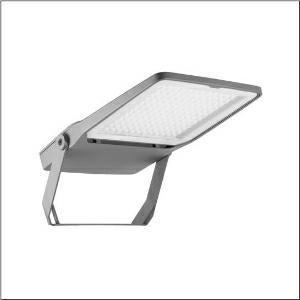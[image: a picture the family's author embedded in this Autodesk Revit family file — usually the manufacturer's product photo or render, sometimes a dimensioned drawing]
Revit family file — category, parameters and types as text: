
# Revit family: floodlight_fl_20_midi___pl61_5xa7681e2c1ac_9e02
name_source: partatom
category: Lighting Fixtures
units: mm (PartAtom-declared; Revit-internal decimal feet)

## family parameters
Cut with Voids When Loaded = No
Host = Face
Light Source = No
Part Type = Normal
Room Calculation Point = No
Round Connector Dimension = Use Diameter
Shared = No

## types (1)
- Floodlight FL 20 midi  PL61 (1 x LED 4000K / CRI = 70 (unbekannt), 27150 lm, 4000K)
    Apparent Load = 208 VA
    CIE Flux Codes = 33 65 98 100 100
    Color Rendering = 70
    Color Temperature = 4000K
    Default Elevation = 1800 mm
    Description = Floodlight FL 20 midi, floodlight, primary light control with lens, of plastic, primary optical cover: protective disc, of toughened safety glass, transparent, light distribution: PL61, light emission: direct distribution, primary light characteristic: asymmetric, installation type: surface-mounted, LED High Power LED, rated luminous flux: 27.150 lm, light colour: 740, colour temperature: 4000K, control gear: ECG Basic, control: power reduction, overheat protection, electronic power reduction, with terminal, 5-pole, max. 2.5mm², mains connection: 220..240V, AC, 50/60Hz, rated input power: 208W, LED unit, of diecast aluminium, powder-coated, Siteco® metallic grey (DB 702S), length: 654 mm, width: 450 mm, height: 76mm, housing frame, of diecast aluminium, powder-coated, Siteco® metallic grey (DB 702S), mounting bracket, of steel, powder-coated, Siteco® metallic grey (DB 702S), ON/OFFprotection rating (complete): IP66, insulation class (complete): insulation class I (protective earthing), certification: CE, ENEC, VDE, protection symbol: D, permissible ambient temperature for indoor applications: -40..+40°C, permissible ambient temperature for outdoor applications: -40..+50°C, standard: DIN EN 12944, packaging unit: 1 piece

Light Distribution: PL61
    Height = 76 mm
    Lamp = 1 x LED 4000K / CRI >= 70 (unbekannt)
    Lamp Light Flux = 27150 lm
    Lamp count = 1
    Length = 672 mm
    Luminous efficacy = 131 lm/W
    Manufacturer = Siteco
    ModVariant = No
    Model = 5XA7681E2C1AC
    Number of Poles = 1
    OnlyDefault = Yes
    Power Factor = 1
    Product Name = Floodlight FL 20 midi | PL61
    Product group = floodlight | pylon top
    ProductGroupID = 6101
    Protection Class = Protection class I
    Protection Degree = IP 66
    RLX_Detail_Level = 1
    RlxData = <blob elided: 94005 chars, md5=0d09d784>
    Socket = socket
    Standby Power = 0 W
    System Light Flux = 27150 lm
    System Power = 208 W
    Type Comments = Product without accessories
    Type Image = l_1005943.jpg
    URL = http://relux.com
    VarID = ---
    Voltage = 0 V
    Weight = 0.00 kg
    Width = 450 mm

## geometry (parser evidence)
native form markers: Blend x4, Sweep x12
no freeform markers — native parametric forms only
